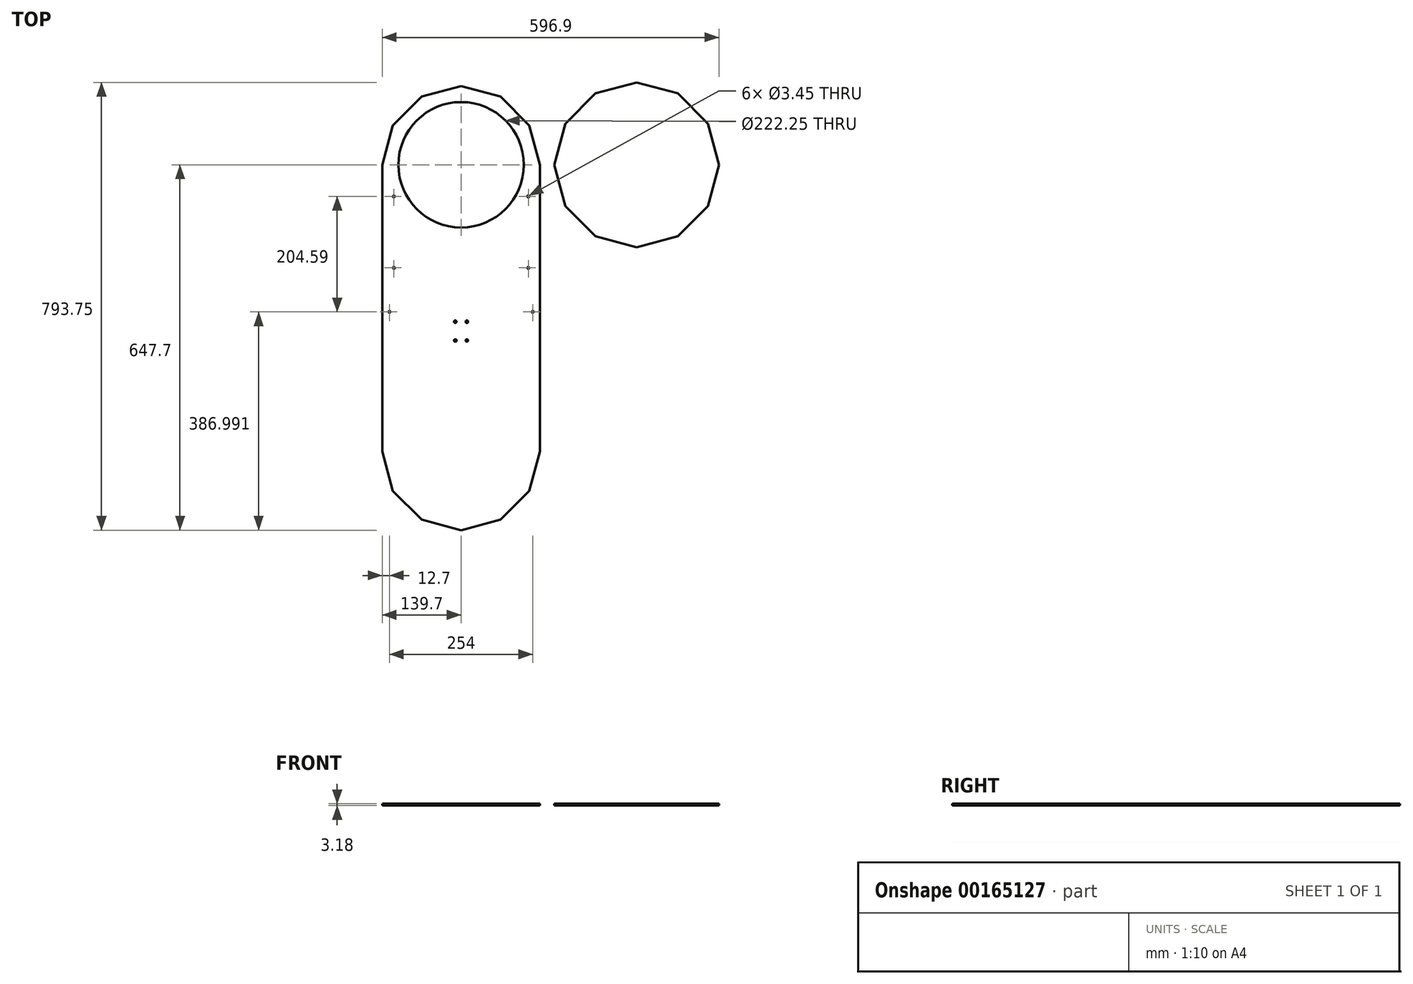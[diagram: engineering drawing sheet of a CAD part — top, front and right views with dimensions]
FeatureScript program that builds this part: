
annotation { "Feature Type Name" : "Feature", "Feature Type Description" : "" }
export const myFeature = defineFeature(function(context is Context, id is Id, definition is map)
    precondition{}
    {
        {
            var Q0;
            Q0=qCreatedBy(makeId("Top.planeOp"),FACE);
            var sketch = newSketch(context, id + "F0", { "sketchPlane" : qUnion([Q0])});
            skLineSegment(sketch, "E0", {"start": v(139.7, 0) * mm, "end": v(279.4, 0) * mm, "construction": true});
            skLineSegment(sketch, "E1", {"start": v(139.7, 0) * mm, "end": v(260.68, 69.85) * mm, "construction": true});
            skLineSegment(sketch, "E2", {"start": v(139.7, 0) * mm, "end": v(209.55, 120.98) * mm, "construction": true});
            skLineSegment(sketch, "E3", {"start": v(139.7, 0) * mm, "end": v(139.7, 139.7) * mm, "construction": true});
            skLineSegment(sketch, "E4", {"start": v(279.4, 0) * mm, "end": v(260.68, 69.85) * mm});
            skLineSegment(sketch, "E5", {"start": v(260.68, 69.85) * mm, "end": v(209.55, 120.98) * mm});
            skLineSegment(sketch, "E6", {"start": v(209.55, 120.98) * mm, "end": v(139.7, 139.7) * mm});
            skLineSegment(sketch, "E7", {"start": v(279.4, 0) * mm, "end": v(279.4, -508) * mm});
            skLineSegment(sketch, "E8", {"start": v(279.4, -508) * mm, "end": v(139.7, -508) * mm, "construction": true});
            skLineSegment(sketch, "E9", {"start": v(139.7, -508) * mm, "end": v(260.68, -577.85) * mm, "construction": true});
            skLineSegment(sketch, "E10", {"start": v(139.7, 0) * mm, "end": v(69.85, 120.98) * mm, "construction": true});
            skLineSegment(sketch, "E11", {"start": v(139.7, 0) * mm, "end": v(18.72, 69.85) * mm, "construction": true});
            skLineSegment(sketch, "E12", {"start": v(139.7, 0) * mm, "end": v(0, 0) * mm, "construction": true});
            skLineSegment(sketch, "E13", {"start": v(139.7, -508) * mm, "end": v(0, -508) * mm, "construction": true});
            skLineSegment(sketch, "E14", {"start": v(139.7, 139.7) * mm, "end": v(69.85, 120.98) * mm});
            skLineSegment(sketch, "E15", {"start": v(69.85, 120.98) * mm, "end": v(18.72, 69.85) * mm});
            skLineSegment(sketch, "E16", {"start": v(18.72, 69.85) * mm, "end": v(0, 0) * mm});
            skLineSegment(sketch, "E17", {"start": v(0, 0) * mm, "end": v(0, -508) * mm});
            skLineSegment(sketch, "E18", {"start": v(139.7, -508) * mm, "end": v(209.55, -628.98) * mm, "construction": true});
            skLineSegment(sketch, "E19", {"start": v(139.7, -508) * mm, "end": v(139.7, -647.7) * mm, "construction": true});
            skLineSegment(sketch, "E20", {"start": v(139.7, -508) * mm, "end": v(69.85, -628.98) * mm, "construction": true});
            skLineSegment(sketch, "E21", {"start": v(139.7, -508) * mm, "end": v(18.72, -577.85) * mm, "construction": true});
            skLineSegment(sketch, "E22", {"start": v(0, -508) * mm, "end": v(18.72, -577.85) * mm});
            skLineSegment(sketch, "E23", {"start": v(18.72, -577.85) * mm, "end": v(69.85, -628.98) * mm});
            skLineSegment(sketch, "E24", {"start": v(69.85, -628.98) * mm, "end": v(139.7, -647.7) * mm});
            skLineSegment(sketch, "E25", {"start": v(139.7, -647.7) * mm, "end": v(209.55, -628.98) * mm});
            skLineSegment(sketch, "E26", {"start": v(209.55, -628.98) * mm, "end": v(260.68, -577.85) * mm});
            skLineSegment(sketch, "E27", {"start": v(260.68, -577.85) * mm, "end": v(279.4, -508) * mm});
            skLineSegment(sketch, "E28", {"start": v(279.4, 0) * mm, "end": v(304.8, 0) * mm, "construction": true});
            skCircle(sketch, "E29.cCircle", {"center": v(450.85, 0) * mm, "radius": 141.07 * mm, "construction": true});
            skLineSegment(sketch, "E29.0", {"start": v(523.88, -126.48) * mm, "end": v(450.85, -146.05) * mm});
            skLineSegment(sketch, "E29.1", {"start": v(450.85, -146.05) * mm, "end": v(377.82, -126.48) * mm});
            skLineSegment(sketch, "E29.2", {"start": v(377.82, -126.48) * mm, "end": v(324.37, -73.03) * mm});
            skLineSegment(sketch, "E29.3", {"start": v(324.37, -73.02) * mm, "end": v(304.8, 0) * mm});
            skLineSegment(sketch, "E29.4", {"start": v(304.8, 0) * mm, "end": v(324.37, 73.02) * mm});
            skLineSegment(sketch, "E29.5", {"start": v(324.37, 73.03) * mm, "end": v(377.83, 126.48) * mm});
            skLineSegment(sketch, "E29.6", {"start": v(377.83, 126.48) * mm, "end": v(450.85, 146.05) * mm});
            skLineSegment(sketch, "E29.7", {"start": v(450.85, 146.05) * mm, "end": v(523.87, 126.48) * mm});
            skLineSegment(sketch, "E29.8", {"start": v(523.88, 126.48) * mm, "end": v(577.33, 73.02) * mm});
            skLineSegment(sketch, "E29.9", {"start": v(577.33, 73.03) * mm, "end": v(596.9, 0) * mm});
            skLineSegment(sketch, "E29.10", {"start": v(596.9, 0) * mm, "end": v(577.33, -73.02) * mm});
            skLineSegment(sketch, "E29.11", {"start": v(577.33, -73.03) * mm, "end": v(523.88, -126.48) * mm});
            skLineSegment(sketch, "E30", {"start": v(304.8, 0) * mm, "end": v(450.85, 0) * mm, "construction": true});
            skLineSegment(sketch, "E31", {"start": v(450.85, 0) * mm, "end": v(450.85, 146.05) * mm, "construction": true});
            skCircle(sketch, "E32", {"center": v(139.7, 0) * mm, "radius": 111.13 * mm});
            skSolve(sketch);
        }
        {
            var Q0;
            Q0=qSketchRegion(id+"F0",true);
            extrude(context, id + "F1", {"entities" : qUnion([Q0]), "depth" : 3.17 * mm});
        }
        {
            var Q0;
            Q0=makeQuery(id+"F1.opExtrude","CAP_FACE",FACE,{"disambiguationData":[OSD([sQuery(id+"F0.wireOp",EDGE,"E4"),sQuery(id+"F0.wireOp",EDGE,"E5"),sQuery(id+"F0.wireOp",EDGE,"E6"),sQuery(id+"F0.wireOp",EDGE,"E7"),sQuery(id+"F0.wireOp",EDGE,"E14"),sQuery(id+"F0.wireOp",EDGE,"E15"),sQuery(id+"F0.wireOp",EDGE,"E16"),sQuery(id+"F0.wireOp",EDGE,"E17"),sQuery(id+"F0.wireOp",EDGE,"E22"),sQuery(id+"F0.wireOp",EDGE,"E23"),sQuery(id+"F0.wireOp",EDGE,"E24"),sQuery(id+"F0.wireOp",EDGE,"E25"),sQuery(id+"F0.wireOp",EDGE,"E26"),sQuery(id+"F0.wireOp",EDGE,"E27")])],"isStart":false});
            var sketch = newSketch(context, id + "F2", { "sketchPlane" : qUnion([Q0])});
            skLineSegment(sketch, "E33", {"start": v(139.7, 139.7) * mm, "end": v(139.7, 114.3) * mm, "construction": true});
            skLineSegment(sketch, "E34", {"start": v(139.7, 114.3) * mm, "end": v(209.55, 95.58) * mm, "construction": true});
            skLineSegment(sketch, "E35", {"start": v(139.7, 114.3) * mm, "end": v(82.55, 98.99) * mm, "construction": true});
            skLineSegment(sketch, "E36", {"start": v(209.55, 120.98) * mm, "end": v(209.55, 95.58) * mm, "construction": true});
            skLineSegment(sketch, "E37", {"start": v(82.55, 98.99) * mm, "end": v(69.85, 120.98) * mm, "construction": true});
            skLineSegment(sketch, "E38.bottom", {"start": v(169.07, 100.08) * mm, "end": v(110.33, 100.08) * mm, "construction": true});
            skLineSegment(sketch, "E38.top", {"start": v(169.07, 41.34) * mm, "end": v(110.33, 41.34) * mm, "construction": true});
            skLineSegment(sketch, "E38.left", {"start": v(169.07, 100.08) * mm, "end": v(169.07, 41.34) * mm, "construction": true});
            skLineSegment(sketch, "E38.right", {"start": v(110.33, 100.08) * mm, "end": v(110.33, 41.34) * mm, "construction": true});
            skPoint(sketch, "E38.middle", {"position": v(139.7, 70.71) * mm});
            skCircle(sketch, "E39", {"center": v(139.7, 70.71) * mm, "radius": 20.64 * mm});
            skLineSegment(sketch, "E40", {"start": v(169.07, 100.08) * mm, "end": v(169.07, 106.43) * mm, "construction": true});
            skLineSegment(sketch, "E41", {"start": v(139.7, 70.71) * mm, "end": v(139.7, 114.3) * mm, "construction": true});
            skLineSegment(sketch, "E42", {"start": v(139.7, 70.71) * mm, "end": v(139.7, -119.42) * mm, "construction": true});
            skLineSegment(sketch, "E43", {"start": v(139.7, -119.42) * mm, "end": v(258.87, -56.12) * mm, "construction": true});
            skLineSegment(sketch, "E44", {"start": v(258.87, -119.42) * mm, "end": v(258.87, -182.72) * mm, "construction": true});
            skLineSegment(sketch, "E45", {"start": v(258.87, -182.72) * mm, "end": v(139.7, -119.42) * mm, "construction": true});
            skLineSegment(sketch, "E46", {"start": v(139.7, -119.42) * mm, "end": v(20.53, -56.12) * mm, "construction": true});
            skLineSegment(sketch, "E47", {"start": v(20.53, -182.72) * mm, "end": v(139.7, -119.42) * mm, "construction": true});
            skCircle(sketch, "E48", {"center": v(258.87, -56.12) * mm, "radius": 1.73 * mm});
            skCircle(sketch, "E49", {"center": v(258.87, -182.72) * mm, "radius": 1.73 * mm});
            skCircle(sketch, "E50", {"center": v(110.33, 41.34) * mm, "radius": 1.73 * mm});
            skCircle(sketch, "E51", {"center": v(169.07, 41.34) * mm, "radius": 1.73 * mm});
            skCircle(sketch, "E52", {"center": v(169.07, 100.08) * mm, "radius": 1.73 * mm});
            skCircle(sketch, "E53", {"center": v(110.33, 100.08) * mm, "radius": 1.73 * mm});
            skCircle(sketch, "E54", {"center": v(20.53, -182.72) * mm, "radius": 1.73 * mm});
            skCircle(sketch, "E55", {"center": v(20.53, -56.12) * mm, "radius": 1.73 * mm});
            skLineSegment(sketch, "E56", {"start": v(139.7, -119.42) * mm, "end": v(258.87, -119.42) * mm, "construction": true});
            skLineSegment(sketch, "E57", {"start": v(139.7, -119.42) * mm, "end": v(20.53, -119.42) * mm, "construction": true});
            skLineSegment(sketch, "E58", {"start": v(20.53, -119.42) * mm, "end": v(20.53, -182.72) * mm, "construction": true});
            skLineSegment(sketch, "E59", {"start": v(20.53, -119.42) * mm, "end": v(20.53, -56.12) * mm, "construction": true});
            skLineSegment(sketch, "E60", {"start": v(258.87, -119.42) * mm, "end": v(258.87, -56.12) * mm, "construction": true});
            skLineSegment(sketch, "E61", {"start": v(139.7, -119.42) * mm, "end": v(139.7, -260.7) * mm, "construction": true});
            skLineSegment(sketch, "E62", {"start": v(12.7, -260.7) * mm, "end": v(266.7, -260.7) * mm, "construction": true});
            skLineSegment(sketch, "E63", {"start": v(266.7, -260.7) * mm, "end": v(279.4, -260.7) * mm, "construction": true});
            skLineSegment(sketch, "E64", {"start": v(139.7, -260.7) * mm, "end": v(139.7, -278.17) * mm, "construction": true});
            skLineSegment(sketch, "E65.bottom", {"start": v(129.38, -278.17) * mm, "end": v(150.02, -278.17) * mm, "construction": true});
            skLineSegment(sketch, "E65.top", {"start": v(129.38, -311.5) * mm, "end": v(150.02, -311.5) * mm, "construction": true});
            skLineSegment(sketch, "E65.left", {"start": v(129.38, -278.17) * mm, "end": v(129.38, -311.5) * mm, "construction": true});
            skLineSegment(sketch, "E65.right", {"start": v(150.02, -278.17) * mm, "end": v(150.02, -311.5) * mm, "construction": true});
            skCircle(sketch, "E66", {"center": v(266.7, -260.7) * mm, "radius": 1.73 * mm});
            skCircle(sketch, "E67", {"center": v(12.7, -260.7) * mm, "radius": 1.73 * mm});
            skCircle(sketch, "E68", {"center": v(150.02, -311.5) * mm, "radius": 2.15 * mm});
            skCircle(sketch, "E69", {"center": v(129.38, -311.5) * mm, "radius": 2.15 * mm});
            skCircle(sketch, "E70", {"center": v(129.38, -278.17) * mm, "radius": 2.15 * mm});
            skCircle(sketch, "E71", {"center": v(150.02, -278.17) * mm, "radius": 2.15 * mm});
            skArc(sketch, "E72", {"start": v(16.33, -184.96) * mm, "mid": v(22.77, -186.93) * mm, "end": v(24.74, -180.5) * mm, "construction": true});
            skArc(sketch, "E73", {"start": v(16.33, -53.89) * mm, "mid": v(0, -119.42) * mm, "end": v(16.33, -184.96) * mm, "construction": true});
            skArc(sketch, "E74", {"start": v(24.74, -58.35) * mm, "mid": v(22.77, -51.91) * mm, "end": v(16.33, -53.89) * mm, "construction": true});
            skSolve(sketch);
        }
        {
            var Q0;
            Q0=qSketchRegion(id+"F2",true);
            var Q1;
            Q1=makeQuery(id+"F1.opExtrude","CAP_FACE",FACE,{"disambiguationData":[OSD([sQuery(id+"F0.wireOp",EDGE,"E4"),sQuery(id+"F0.wireOp",EDGE,"E5"),sQuery(id+"F0.wireOp",EDGE,"E6"),sQuery(id+"F0.wireOp",EDGE,"E7"),sQuery(id+"F0.wireOp",EDGE,"E14"),sQuery(id+"F0.wireOp",EDGE,"E15"),sQuery(id+"F0.wireOp",EDGE,"E16"),sQuery(id+"F0.wireOp",EDGE,"E17"),sQuery(id+"F0.wireOp",EDGE,"E22"),sQuery(id+"F0.wireOp",EDGE,"E23"),sQuery(id+"F0.wireOp",EDGE,"E24"),sQuery(id+"F0.wireOp",EDGE,"E25"),sQuery(id+"F0.wireOp",EDGE,"E26"),sQuery(id+"F0.wireOp",EDGE,"E27")])],"isStart":true});
            extrude(context, id + "F3", {"entities" : qUnion([Q0]), "operationType" : NewBodyOperationType.REMOVE, "endBound" : BoundingType.UP_TO_SURFACE, "oppositeDirection" : true, "endBoundEntityFace" : qUnion([Q1]), "depth" : 25.4 * mm});
        }
    });
